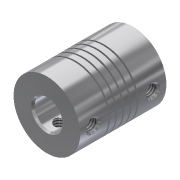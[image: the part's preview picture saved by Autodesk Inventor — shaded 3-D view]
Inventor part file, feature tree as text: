
AUTODESK INVENTOR PART (.ipt)
format: ipt  version: 2014 (Build 180170000, 170)  size: 298,496 bytes
history: native  units: in
note: dims shown in document units (in); Inventor stores cm internally (conversion verified against a paired STEP export)
features: sketch x5, extrude x2, hole x2, chamfer x2, helix x1, plane x1, other x1
ambient origin geometry x8: Origin, YZ Plane, XZ Plane, XY Plane, X Axis, Y Axis, Z Axis, Center Point
bodies: Solid1 (feature_tree)
feature tree (14):
  sketch  "Sketch1"  dims[d0=0.75in d1=0.1969in]
  extrude  "Extrusion1"  Depth=0.1969in
  extrude  "Extrusion2"  Depth=0.315in
  helix  "Coil1"  [1 undecoded]
  hole  "Hole1"  [1 undecoded]
  plane  "Work Plane2"
  hole  "Hole2"  [1 undecoded]
  chamfer  "Chamfer1"  Distance=0.1575in
  chamfer  "Chamfer2"  Distance=0.15in
  sketch  "Sketch3"  dims[d2=0.97in d3=0.0in d4=0.315in d5=0.69in d6=0.0in]
  sketch  "Sketch5"  dims[d8=0.017in]
  sketch  "Sketch6"  dims[d9=0.08in d10=1.0in d11=1.9685in d12=0.0in d13=90.0deg d14=90.0deg d15=0.0in d16=0.0in d17=0.277in]
  other  "Work Axis1"
  sketch  "Sketch8"  dims[d18=0.1575in d19=0.15in d20=0.1575in d21=0.15in d22=0.128in d23=0.75in d24=0.375in d25=0.25in d26=0.5635in d27=1.0in d28=0.8108in d29=90.0deg d30=0.1575in d31=0.1575in d32=0.15in d33=0.1496in d34=0.128in d35=0.75in d36=0.375in d37=0.25in d38=0.5635in d39=1.0in d40=0.8108in d41=0.0197in d42=0.125in d43=45.0deg d44=0.0197in d45=0.125in d46=45.0deg]
note: 3 required parameter values undecoded (feature->parameter linkage not recoverable at this tier; creation-order binding heuristic only, values carry confidence <= 0.55)
